# Revit family: Lighting-Luminii-Leto_44_Mini_Wet_S
name_source: partatom
category: Lighting Fixtures
units: mm (PartAtom-declared; Revit-internal decimal feet)

## family parameters
Cut with Voids When Loaded = No
Host = Face
Light Source = Yes
Maintain Annotation Orientation = No
OmniClass Number = 23.80.70.11.14.21
OmniClass Title = Spots and Tracklight Specialties
Part Type = Normal
Room Calculation Point = No
Round Connector Dimension = Use Diameter
Shared = Yes

## types (3) — shared parameters
Apparent Load = 14 VA
Assembly Code = D5020230
CCT = 3500K
Color Filter = 16777215
Control Type = Consult Manufacturer Website for more Information
Control Zone = Consult Manufacturer Website for more Information
Current Amps = 50 A
Depth = 2.5 "
Description = Surface Mount LED Downlight
Dimming Lamp Color Temperature Shift = <None>
Dimming Type = Consult Manufacturer Website for more Information
Environment = Indoor
Finish = Metal - Luminii - Silver Anodized Aluminum
Frequency = 60 Hz
Has Battery Backup = No
Has Dimming = Yes
Housing Protection Rating = Consult Manufacturer Website for more Information
Initial Color Comments = Perfomance based on 3500K Photometric Web File
Keynote = 26 50 00
Lamp = LED
Lamp Life = 1
Lens Material = Plastic - Luminii - Frosted Lens
Load Classification = Lighting
Luminaire Type = Surface LED Light
Manufacturer = Luminii
Mounting Method = Surface Mounted
Number of Poles = 1
Operating Temperature = Consult Manufacturer Website for more Information
Phase = 1
Photometric Web File = LET44MW-XX-L-10-35K-F20-NA.ies
Power Factor = 1
Power Source Type = Driver
Product Page URL = https://www.luminii.com
Tilt Angle = -90.00°
URL = https://www.luminii.com
Version = 2020 - v1.0a
Voltage = 120 V
Voltage Comments = 120V | 277V | 347V
Warranty URL = https://www.luminii.com
Wattage Comments = 13.6W
Width = 2.5 "
zero-valued in all types: Default Elevation

## per-type parameters (varying)
| type | Constraints | Model |
| Large | 3 | 657-L |
| Medium | 2 | 657-M |
| Small | 1 | 657-S |

## geometry (parser evidence)
native form markers: Sweep x4
no freeform markers — native parametric forms only
